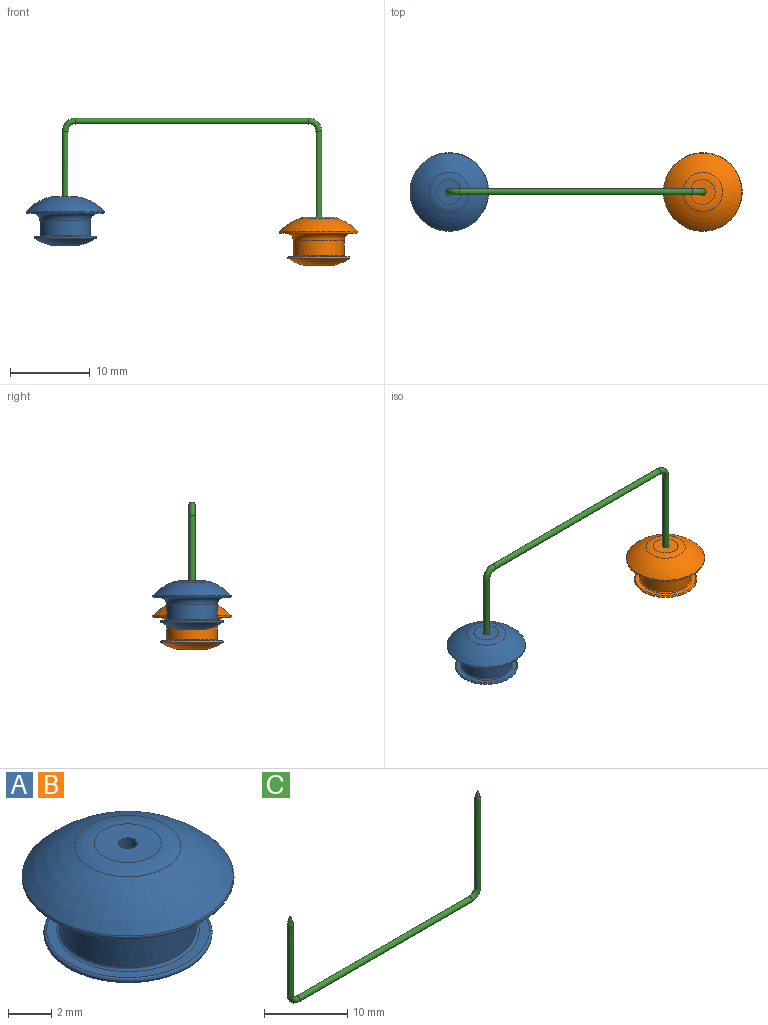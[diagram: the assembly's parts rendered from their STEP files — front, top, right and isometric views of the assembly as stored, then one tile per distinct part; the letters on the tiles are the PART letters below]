
ASSEMBLY  parts=3 mates=2
PART A: 15 faces, bbox 10.7x10.7x6.1 mm
  f0: torus R=0.2mm, axis (0,0,1), area 69.7mm2, adj f9,f13
  f1: plane 3.11x3.11mm, normal (0,0,1), area 7mm2, adj f11,f13
  f2: plane 2.57x2.57mm, normal (0,0,-1), area 5.2mm2, adj f14
  f3: torus R=0.59mm, axis (0,0,1), area 39.9mm2, adj f7,f14
  f4: plane 7.56x7.56mm, normal (0,0,1), area 10.5mm2, adj f7,f8
  f5: cylinder r=3.17mm len=6.35mm, axis (0,0,1), area 37.4mm2, adj f8,f12
  f6: plane 9.58x9.58mm, normal (0,0,-1), area 19.5mm2, adj f9,f12
  f7: torus R=3.78mm, axis (0,0,1), area 8.2mm2, adj f3,f4
  f8: torus R=3.31mm, axis (0,0,1), area 4.2mm2, adj f4,f5
  f9: torus R=4.79mm, axis (0,0,-1), area 9.3mm2, adj f0,f6
  f10: cone r=0mm half-angle=59deg, axis (0,0,1), area 0.7mm2, adj f11
  f11: cylinder r=0.43mm len=3.3mm, axis (0,0,1), area 9mm2, adj f1,f10
  f12: torus R=4.09mm, axis (0,0,-1), area 31.9mm2, adj f5,f6
  f13: torus R=1.55mm, axis (0,0,-1), area 11.6mm2, adj f0,f1
  f14: torus R=1.29mm, axis (0,0,-1), area 5.1mm2, adj f2,f3
PART B: same geometry as A
PART C: 13 faces, bbox 32.8x0.8x15.8 mm
  f0: cylinder r=0.38mm len=10.03mm, axis (0,0,-1), area 24mm2, adj f1,f11
  f1: torus R=1.27mm, axis (0,-1,0), area 4.8mm2, adj f0,f2
  f2: cylinder r=0.38mm len=29.21mm, axis (1,0,0), area 69.9mm2, adj f1,f3
  f3: torus R=1.27mm, axis (0,-1,0), area 4.8mm2, adj f2,f4
  f4: cylinder r=0.38mm len=12.57mm, axis (0,0,1), area 30.1mm2, adj f3,f12
  f5: plane 0.05x0.05mm, normal (0,0,1), area 0mm2, adj f10
  f6: cone r=0.38mm half-angle=17.4deg, axis (0,0,-1), area 0.7mm2, adj f10,f11
  f7: plane 0.05x0.05mm, normal (0,0,1), area 0mm2, adj f9
  f8: cone r=0.38mm half-angle=17.4deg, axis (0,0,-1), area 0.7mm2, adj f9,f12
  f9: torus R=0.02mm, axis (0,0,1), area 0mm2, adj f7,f8
  f10: torus R=0.02mm, axis (0,0,1), area 0mm2, adj f5,f6
  f11: revolved ~0.76x0.76mm, area 3.3mm2, adj f0,f6
  f12: revolved ~0.76x0.76mm, area 3.3mm2, adj f4,f8
PLACE A t=(0,0,-0.1)mm
PLACE B t=(31.75,0,-2.64)mm
PLACE C rot(axis=(1,0,0),180deg) t=(15.88,0,15.58)mm
MATE fastened A.f0 <-> C.f0  axis (0,0,1) through (0,0,4.29)mm
MATE fastened B.f0 <-> C.f4  axis (0,0,1) through (31.75,0,1.75)mm
